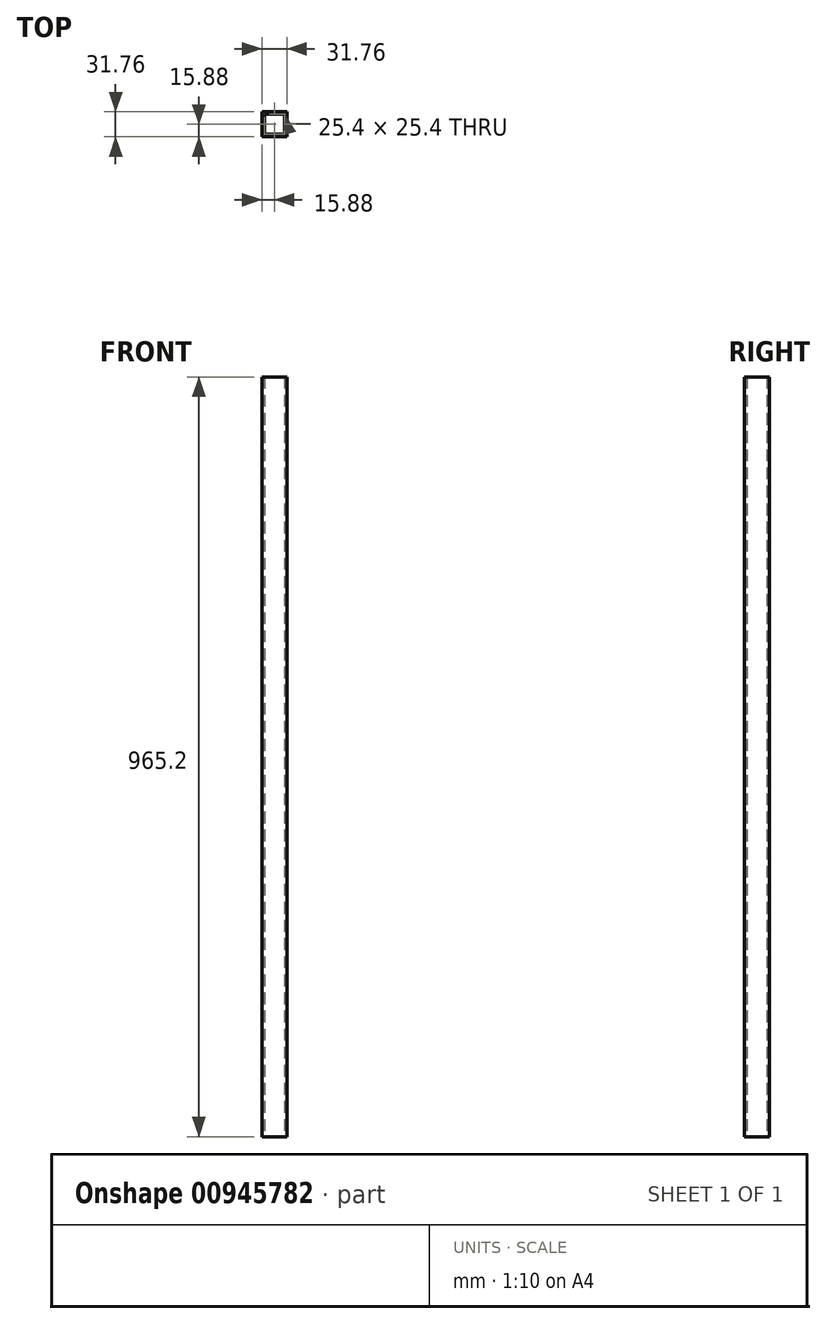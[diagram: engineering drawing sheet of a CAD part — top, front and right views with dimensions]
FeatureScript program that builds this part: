
annotation { "Feature Type Name" : "Feature", "Feature Type Description" : "" }
export const myFeature = defineFeature(function(context is Context, id is Id, definition is map)
    precondition{}
    {
        {
            var Q0;
            Q0=qCreatedBy(makeId("Top.planeOp"),FACE);
            var sketch = newSketch(context, id + "F0", { "sketchPlane" : qUnion([Q0])});
            skLineSegment(sketch, "E0.bottom", {"start": v(12.7, 12.7) * mm, "end": v(-12.7, 12.7) * mm});
            skLineSegment(sketch, "E0.top", {"start": v(12.7, -12.7) * mm, "end": v(-12.7, -12.7) * mm});
            skLineSegment(sketch, "E0.left", {"start": v(12.7, 12.7) * mm, "end": v(12.7, -12.7) * mm});
            skLineSegment(sketch, "E0.right", {"start": v(-12.7, 12.7) * mm, "end": v(-12.7, -12.7) * mm});
            skPoint(sketch, "E0.middle", {"position": v(0, 0) * mm});
            skLineSegment(sketch, "E1.0", {"start": v(15.88, -15.88) * mm, "end": v(-15.88, -15.88) * mm});
            skLineSegment(sketch, "E1.1", {"start": v(15.88, 15.88) * mm, "end": v(15.88, -15.88) * mm});
            skLineSegment(sketch, "E1.2", {"start": v(15.88, 15.88) * mm, "end": v(-15.88, 15.88) * mm});
            skLineSegment(sketch, "E1.3", {"start": v(-15.88, 15.88) * mm, "end": v(-15.88, -15.88) * mm});
            skSolve(sketch);
        }
        {
            var Q0;
            Q0=qSketchRegion(id+"F0",true);
            extrude(context, id + "F1", {"entities" : qUnion([Q0]), "depth" : 965.2 * mm, "offsetDistance" : 25.4 * mm});
        }
    });
